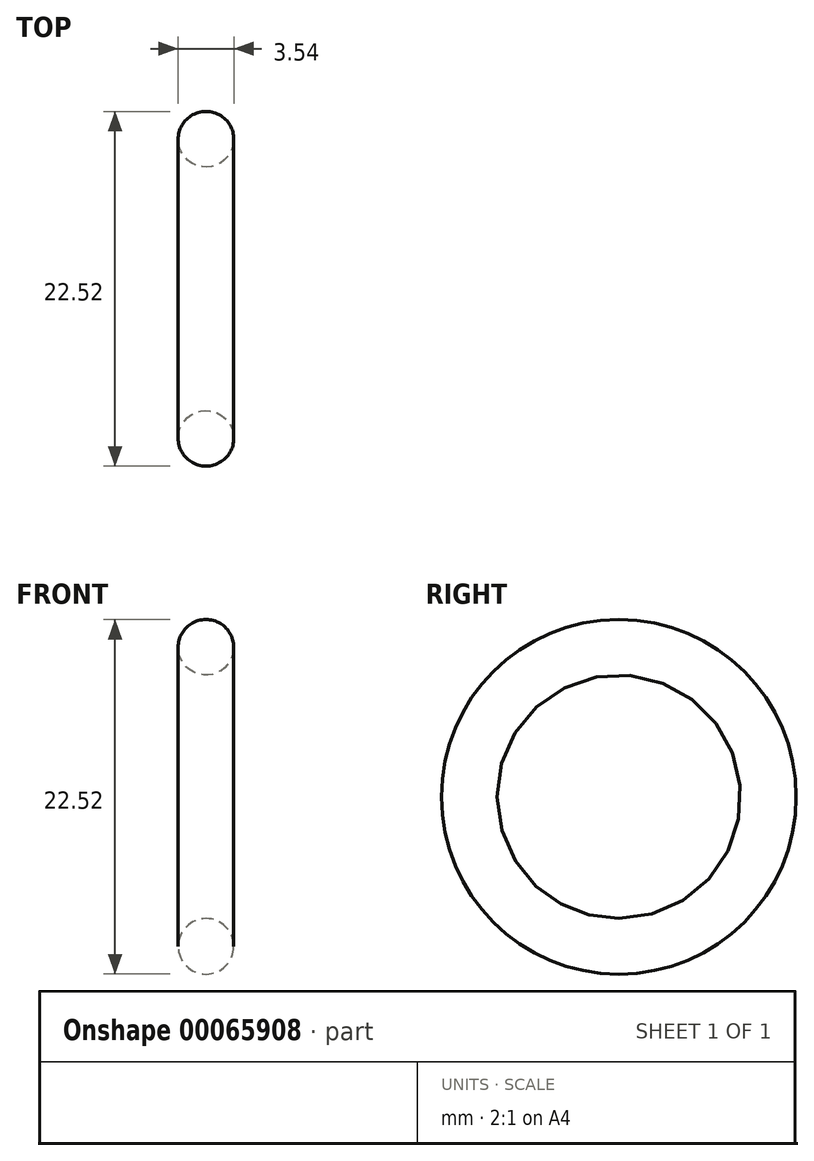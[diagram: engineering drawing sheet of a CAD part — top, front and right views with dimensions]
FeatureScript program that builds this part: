
annotation { "Feature Type Name" : "Feature", "Feature Type Description" : "" }
export const myFeature = defineFeature(function(context is Context, id is Id, definition is map)
    precondition{}
    {
        {
            var Q0;
            Q0=qCreatedBy(makeId("Front.planeOp"),FACE);
            var sketch = newSketch(context, id + "F0", { "sketchPlane" : qUnion([Q0])});
            skLineSegment(sketch, "E0", {"start": v(0, 0) * mm, "end": v(-6.06, 0) * mm, "construction": true});
            skCircle(sketch, "E1", {"center": v(0, 9.5) * mm, "radius": 1.77 * mm});
            skSolve(sketch);
        }
        {
            var Q0;
            Q0=makeQuery(id+"F0.imprint","IMPRINT",FACE,{"disambiguationData":[TD([[makeQuery(id+"F0.imprint","IMPRINT",EDGE,{"derivedFrom":sQuery(id+"F0.wireOp",EDGE,"E1")}),1.0]])]});
            var Q1;
            Q1=sQuery(id+"F0.wireOp",EDGE,"E0");
            revolve(context, id + "F1", {"entities" : qUnion([Q0]), "axis" : qUnion([Q1]), "revolveType" : RevolveType.FULL});
        }
    });
